# Revit family: VENTS-VS_EC
name_source: partatom
category: Mechanical Equipment
units: mm (PartAtom-declared; Revit-internal decimal feet)

## family parameters
Always vertical = Yes
Classification = None
Cut with Voids When Loaded = No
OmniClass Number = 23.75.35.17.11
OmniClass Title = Fans for Air Ductwork
Part Type = Breaks Into
Room Calculation Point = No
Round Connector Dimension = Use Diameter
Shared = No
Work Plane-Based = No

## types (7) — shared parameters
Casing Material = Fan Zinc
Description = Inline centrifugal fan in sound insulated casing
Family Version = 1.0
Load Classification = HVAC
Maintenance Zone Material = Maintenance Zone
Manufacturer = Vents
Plastic Material = Polypropylene Black
Power Factor = 1
Protection rating = IPX4
URL = https://ventilation-system.com
eH = 80 mm  [stored 0.262467 ft]
eL = 80 mm  [stored 0.262467 ft]

## per-type parameters (varying)
| type | A | Apparent Power | Connection H | Connection W | Current | Din | Maintenance Zone Depth | Maximum Air Flow Directly | Maximum Air Flow Perpendicularly | Noise Level at 3 m (dBa) | Number of Poles | Power | RPM (min-1) | Transported Air Temperature (°C) | Type Comments | Voltage | Weight | conA | gsD |
| VS 315 ЕС | 500 mm  [stored 1.64042 ft] | 150 VA | 445 mm  [stored 1.45997 ft] | 445 mm  [stored 1.45997 ft] | 1 A | 250 mm  [stored 0.82021 ft] | 500 mm  [stored 1.64042 ft] | 2252 m³/h | 2370 m³/h | 35 | 1 | 150 W | 1600 | -40...+80 | Inline centrifugal fan VS 315 ЕС | 230 V | 25.70 kg | 250 mm  [stored 0.82021 ft] | 250 mm  [stored 0.82021 ft] |
| VS 355 ЕС | 500 mm  [stored 1.64042 ft] | 250 VA | 445 mm  [stored 1.45997 ft] | 445 mm  [stored 1.45997 ft] | 1 A | 250 mm  [stored 0.82021 ft] | 500 mm  [stored 1.64042 ft] | 3639 m³/h | 3830 m³/h | 44 | 1 | 250 W | 1450 | -25...+60 | Inline centrifugal fan VS 355 ЕС | 230 V | 29.30 kg | 250 mm  [stored 0.82021 ft] | 250 mm  [stored 0.82021 ft] |
| VS 400 ЕС | 670 mm  [stored 2.19816 ft] | 500 VA | 615 mm  [stored 2.01772 ft] | 615 mm  [stored 2.01772 ft] | 2 A | 335 mm  [stored 1.09908 ft] | 670 mm  [stored 2.19816 ft] | 5377 m³/h | 5660 m³/h | 39 | 1 | 500 W | 1500 | -25...+50 | Inline centrifugal fan VS 400 ЕС | 230 V | 42.20 kg | 335 mm  [stored 1.09908 ft] | 335 mm  [stored 1.09908 ft] |
| VS 450 ЕС | 670 mm  [stored 2.19816 ft] | 750 VA | 615 mm  [stored 2.01772 ft] | 615 mm  [stored 2.01772 ft] | 3 A | 335 mm  [stored 1.09908 ft] | 670 mm  [stored 2.19816 ft] | 6460 m³/h | 6800 m³/h | 50 | 1 | 750 W | 1440 | -25...+60 | Inline centrifugal fan VS 450 ЕС | 230 V | 46.30 kg | 335 mm  [stored 1.09908 ft] | 335 mm  [stored 1.09908 ft] |
| VS 500 ЕС | 670 mm  [stored 2.19816 ft] | 1320 VA | 615 mm  [stored 2.01772 ft] | 615 mm  [stored 2.01772 ft] | 2 A | 335 mm  [stored 1.09908 ft] | 670 mm  [stored 2.19816 ft] | 9928 m³/h | 10450 m³/h | 45 | 3 | 1320 W | 1350 | -20...+50 | Inline centrifugal fan VS 500 ЕС | 400 V | 50.00 kg | 335 mm  [stored 1.09908 ft] | 335 mm  [stored 1.09908 ft] |
| VS 560 ЕС | 800 mm  [stored 2.62467 ft] | 2360 VA | 745 mm  [stored 2.44423 ft] | 745 mm  [stored 2.44423 ft] | 4 A | 400 mm  [stored 1.31234 ft] | 800 mm  [stored 2.62467 ft] | 12920 m³/h | 13600 m³/h | 50 | 3 | 2360 W | 1540 | -25...+60 | Inline centrifugal fan VS 560 ЕС | 400 V | 60.50 kg | 400 mm  [stored 1.31234 ft] | 400 mm  [stored 1.31234 ft] |
| VS 630 ЕС | 800 mm  [stored 2.62467 ft] | 2750 VA | 745 mm  [stored 2.44423 ft] | 745 mm  [stored 2.44423 ft] | 4 A | 400 mm  [stored 1.31234 ft] | 800 mm  [stored 2.62467 ft] | 15903 m³/h | 16740 m³/h | 50 | 3 | 2750 W | 1300 | -25...+55 | Inline centrifugal fan VS 630 ЕС | 400 V | 69.00 kg | 400 mm  [stored 1.31234 ft] | 400 mm  [stored 1.31234 ft] |

note: column(s) folded — value = type name in every type: Model

note: [stored X ft] marks values corroborated as IEEE doubles in the binary element streams (Revit-internal decimal feet)

## geometry (parser evidence)
native form markers: Sweep x11
no freeform markers — native parametric forms only
